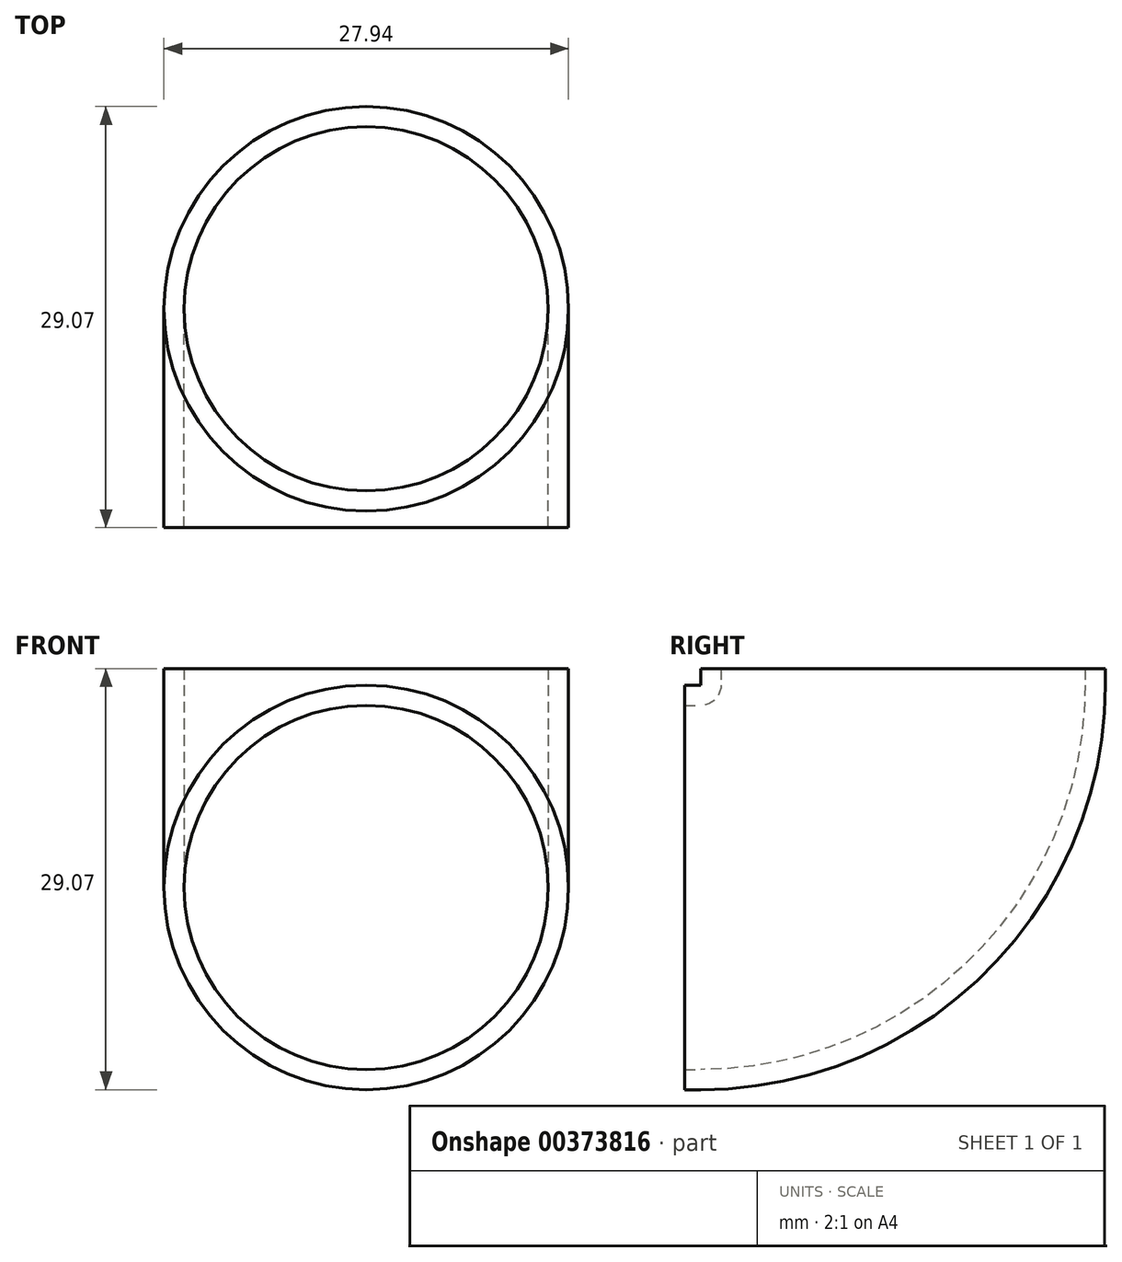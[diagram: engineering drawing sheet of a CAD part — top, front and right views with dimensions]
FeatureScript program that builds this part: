
annotation { "Feature Type Name" : "Feature", "Feature Type Description" : "" }
export const myFeature = defineFeature(function(context is Context, id is Id, definition is map)
    precondition{}
    {
        {
            assignVariable(context, id + "F0", {"name" : "Length", "anyValue" : 1.12});
        }
        {
            var Q0;
            Q0=qCreatedBy(makeId("Front.planeOp"),FACE);
            var sketch = newSketch(context, id + "F1", { "sketchPlane" : qUnion([Q0])});
            skCircle(sketch, "E0", {"center": v(0, 0) * mm, "radius": 12.57 * mm});
            skCircle(sketch, "E1.0", {"center": v(0, 0) * mm, "radius": 13.97 * mm});
            skLineSegment(sketch, "E2", {"start": v(-17.1, 13.97) * mm, "end": v(13.54, 13.97) * mm, "construction": true});
            skSolve(sketch);
        }
        {
            var Q0;
            Q0=makeQuery(id+"F1.imprint","IMPRINT",FACE,{"disambiguationData":[TD([[makeQuery(id+"F1.imprint","IMPRINT",EDGE,{"derivedFrom":sQuery(id+"F1.wireOp",EDGE,"E0")}),-1.0]])]});
            extrude(context, id + "F2", {"entities" : qUnion([Q0]), "depth" : (getVariable(context, 'Length')) * mm});
        }
        {
            var Q0;
            Q0=makeQuery(id+"F1.imprint","IMPRINT",FACE,{"disambiguationData":[TD([[makeQuery(id+"F1.imprint","IMPRINT",EDGE,{"derivedFrom":sQuery(id+"F1.wireOp",EDGE,"E0")}),-1.0]])]});
            var Q1;
            Q1=sQuery(id+"F1.wireOp",EDGE,"E2");
            revolve(context, id + "F3", {"operationType" : NewBodyOperationType.ADD, "entities" : qUnion([Q0]), "axis" : qUnion([Q1]), "revolveType" : RevolveType.ONE_DIRECTION, "angle" : 90 * degree});
        }
        {
            var Q0;
            Q0=makeQuery(id+"F3.opRevolve","CAP_FACE",FACE,{"disambiguationData":[OSD([sQuery(id+"F1.wireOp",EDGE,"E0"),sQuery(id+"F1.wireOp",EDGE,"E1.0")])],"isStart":false});
            extrude(context, id + "F4", {"entities" : qUnion([Q0]), "operationType" : NewBodyOperationType.ADD, "depth" : (getVariable(context, 'Length')) * mm});
        }
    });
